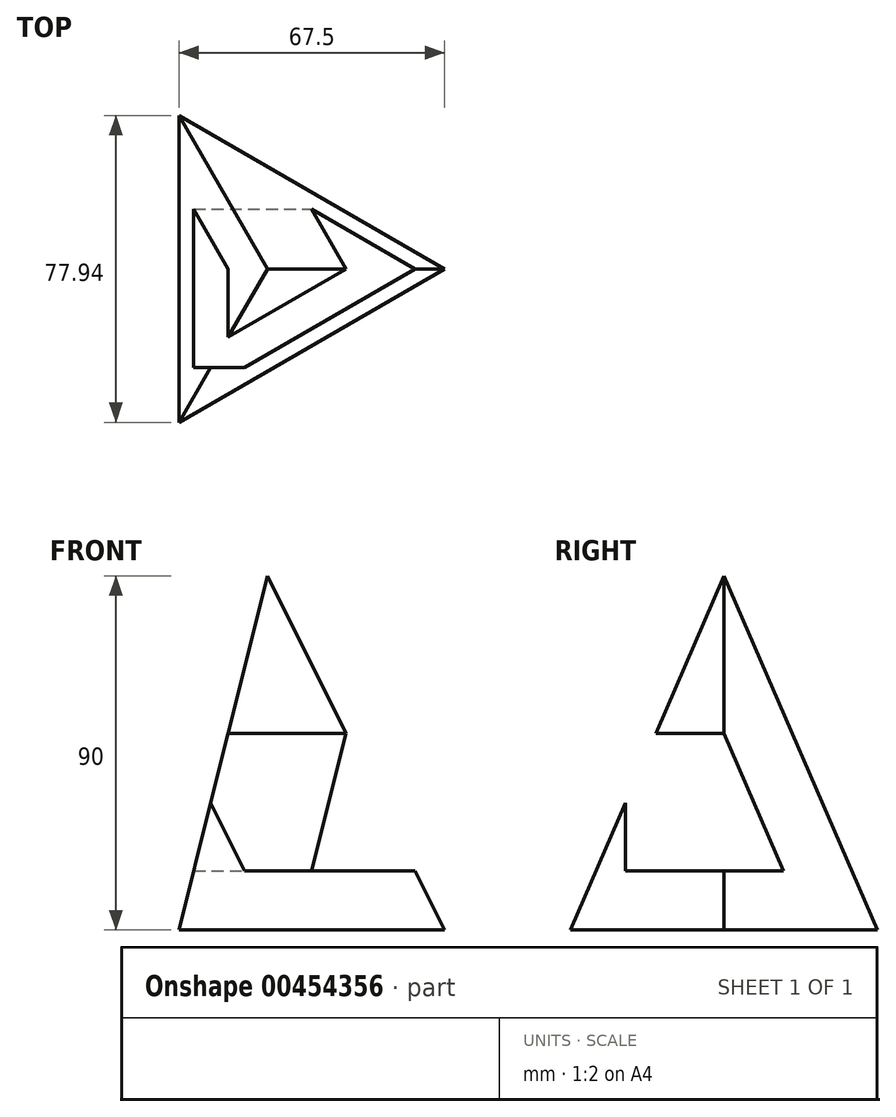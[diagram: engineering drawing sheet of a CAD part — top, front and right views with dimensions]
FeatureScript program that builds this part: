
annotation { "Feature Type Name" : "Feature", "Feature Type Description" : "" }
export const myFeature = defineFeature(function(context is Context, id is Id, definition is map)
    precondition{}
    {
        {
            var Q0;
            Q0=qCreatedBy(makeId("Top.planeOp"),FACE);
            var sketch = newSketch(context, id + "F0", { "sketchPlane" : qUnion([Q0])});
            skCircle(sketch, "E0", {"center": v(0, 0) * mm, "radius": 45 * mm, "construction": true});
            skLineSegment(sketch, "E1", {"start": v(-22.5, 38.97) * mm, "end": v(45, 0) * mm});
            skLineSegment(sketch, "E2", {"start": v(45, 0) * mm, "end": v(-22.5, -38.97) * mm});
            skLineSegment(sketch, "E3", {"start": v(-22.5, -38.97) * mm, "end": v(-22.5, 38.97) * mm});
            skSolve(sketch);
        }
        {
            var Q0;
            Q0=qCreatedBy(makeId("Front.planeOp"),FACE);
            var sketch = newSketch(context, id + "F1", { "sketchPlane" : qUnion([Q0])});
            skLineSegment(sketch, "E4", {"start": v(0, 0) * mm, "end": v(0, 90) * mm});
            skSolve(sketch);
        }
        {
            var Q0;
            Q0=makeQuery(id+"F0.imprint","IMPRINT",FACE,{"disambiguationData":[TD([[makeQuery(id+"F0.imprint","IMPRINT",EDGE,{"derivedFrom":sQuery(id+"F0.wireOp",EDGE,"E1")}),-1.0]])]});
            var Q1;
            Q1=sQuery(id+"F1.wireOp",VERTEX,"E4.end");
            loft(context, id + "F2", {"sheetProfilesArray" : [{ "sheetProfileEntities" : qUnion([Q0]) }, { "sheetProfileEntities" : qUnion([Q1]) }]});
        }
        {
            var Q0;
            Q0=qCreatedBy(makeId("Right.planeOp"),FACE);
            var sketch = newSketch(context, id + "F3", { "sketchPlane" : qUnion([Q0])});
            skLineSegment(sketch, "E5", {"start": v(0, 50) * mm, "end": v(15.16, 15) * mm});
            skLineSegment(sketch, "E6", {"start": v(15.16, 15) * mm, "end": v(-25, 15) * mm});
            skLineSegment(sketch, "E7", {"start": v(-25, 15) * mm, "end": v(-25, 50) * mm});
            skLineSegment(sketch, "E8", {"start": v(-25, 50) * mm, "end": v(0, 50) * mm});
            skSolve(sketch);
        }
        {
            var Q0;
            Q0 = qSketchRegion(id + "F3", true);
            extrude(context, id + "F4", {"entities" : qUnion([Q0]), "operationType" : NewBodyOperationType.REMOVE, "endBound" : BoundingType.THROUGH_ALL, "oppositeDirection" : true, "depth" : 25 * mm, "hasSecondDirection" : true, "secondDirectionBound" : SecondDirectionBoundingType.THROUGH_ALL, "secondDirectionOppositeDirection" : false, "secondDirectionDepth" : 25 * mm});
        }
    });
